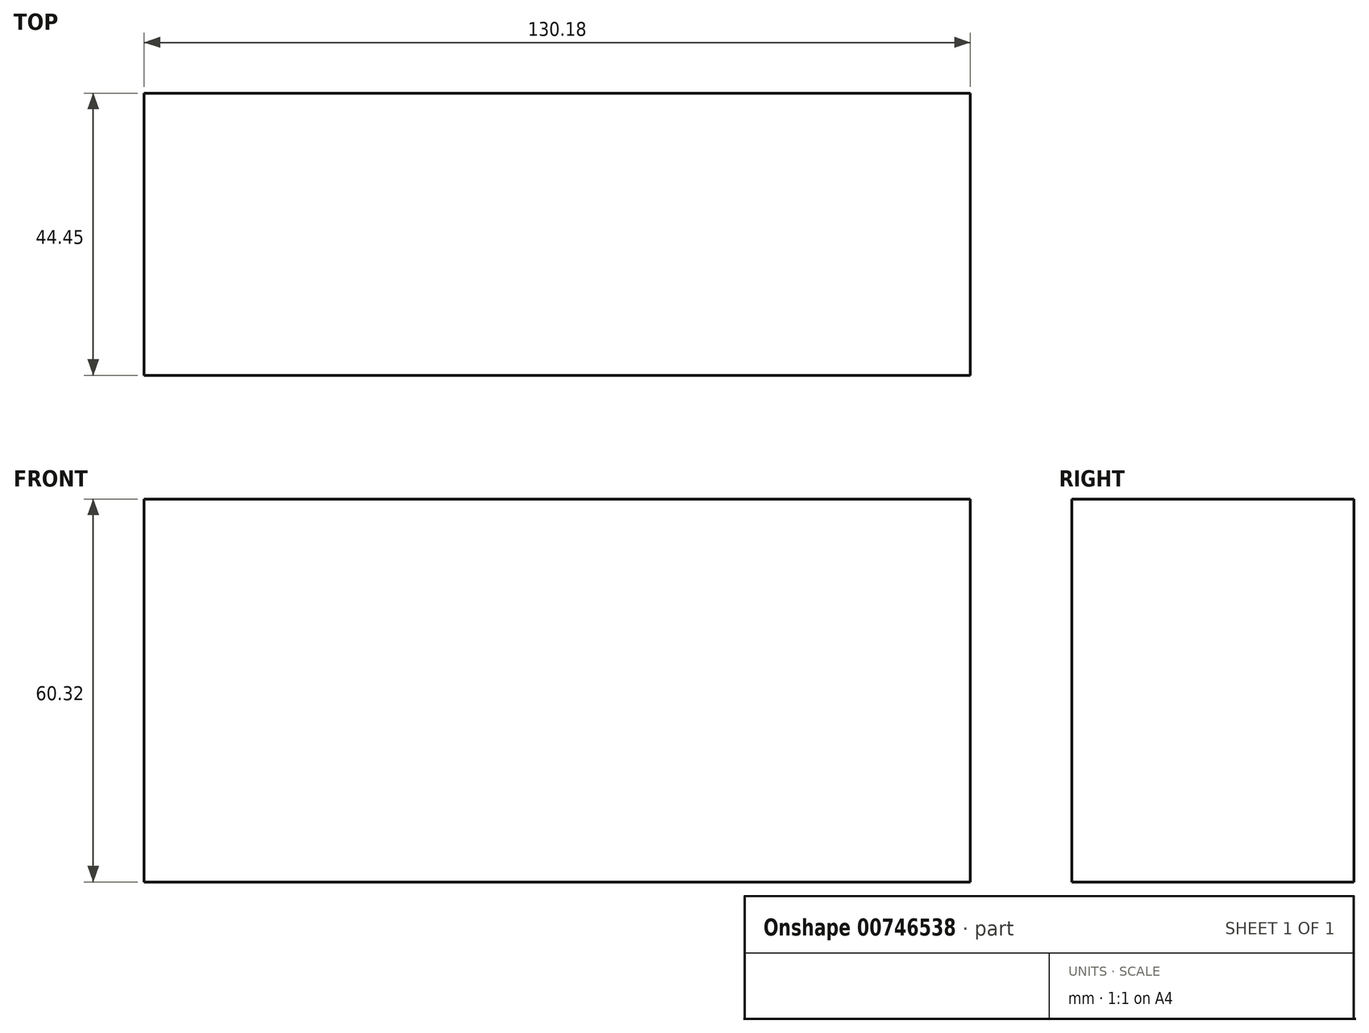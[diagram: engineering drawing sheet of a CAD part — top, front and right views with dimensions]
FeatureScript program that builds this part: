
annotation { "Feature Type Name" : "Feature", "Feature Type Description" : "" }
export const myFeature = defineFeature(function(context is Context, id is Id, definition is map)
    precondition{}
    {
        {
            var Q0;
            Q0=qCreatedBy(makeId("Front.planeOp"),FACE);
            var sketch = newSketch(context, id + "F0", { "sketchPlane" : qUnion([Q0])});
            skLineSegment(sketch, "E0", {"start": v(0, 0) * mm, "end": v(-130.18, 0) * mm});
            skLineSegment(sketch, "E1", {"start": v(-130.18, 0) * mm, "end": v(-130.18, 60.32) * mm});
            skLineSegment(sketch, "E2", {"start": v(-130.18, 60.32) * mm, "end": v(0, 60.32) * mm});
            skLineSegment(sketch, "E3", {"start": v(0, 60.32) * mm, "end": v(0, 0) * mm});
            skSolve(sketch);
        }
        {
            var Q0;
            Q0 = qSketchRegion(id + "F0", true);
            extrude(context, id + "F1", {"entities" : qUnion([Q0]), "depth" : 44.45 * mm, "offsetDistance" : 25.4 * mm});
        }
    });
